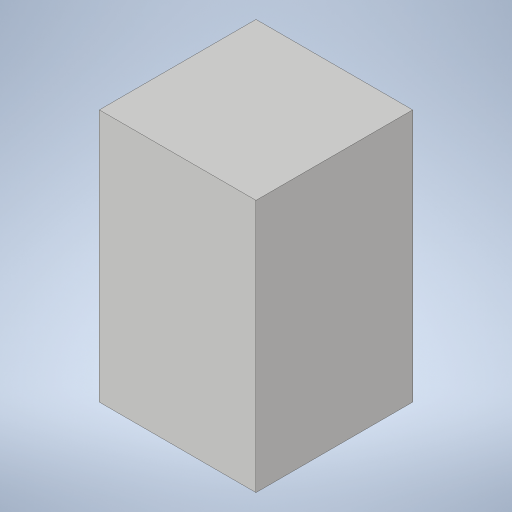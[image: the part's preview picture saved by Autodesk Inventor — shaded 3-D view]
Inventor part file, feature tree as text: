
AUTODESK INVENTOR PART (.ipt)
format: ipt  version: 2023.4 (Build 274418000, 418)  size: 173,568 bytes
history: native  units: in
note: dims shown in document units (in); Inventor stores cm internally (conversion verified against a paired STEP export)
features: extrude x1, sketch x1
ambient origin geometry x8: Origin, YZ Plane, XZ Plane, XY Plane, X Axis, Y Axis, Z Axis, Center Point
bodies: Solid1 (feature_tree)
feature tree (2):
  extrude  "Extrusion1"  Depth=42.0in
  sketch  "Sketch1"  dims[d0=26.0in d1=42.0in d2=26.0in d3=0.0in]
